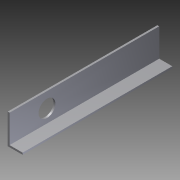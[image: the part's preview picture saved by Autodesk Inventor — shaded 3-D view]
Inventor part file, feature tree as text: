
AUTODESK INVENTOR PART (.ipt)
format: ipt  version: 2012 (Build 160160000, 160)  size: 86,016 bytes
history: native  units: in
note: dims shown in document units (in); Inventor stores cm internally (conversion verified against a paired STEP export)
features: extrude x2, sketch x2
ambient origin geometry x8: Origin, YZ Plane, XZ Plane, XY Plane, X Axis, Y Axis, Z Axis, Center Point
bodies: Solid1 (feature_tree)
feature tree (4):
  extrude  "Extrusion1"  Depth=1.0in
  extrude  "Extrusion2"  Depth=0.125in
  sketch  "Sketch1"  dims[d0=2.0in d1=1.0in]
  sketch  "Sketch2"  dims[d2=0.125in d3=0.125in d4=10.0in d5=0.0in d6=1.125in d8=1.0in d9=4.0in d10=0.0in d11=2.5in]
